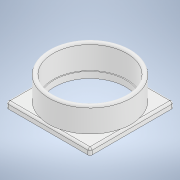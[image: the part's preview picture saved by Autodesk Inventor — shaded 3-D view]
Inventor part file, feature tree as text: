
AUTODESK INVENTOR PART (.ipt)
format: ipt  version: 2022 (Build 260153000, 153)  size: 171,520 bytes
history: native  units: in
note: dims shown in document units (in); Inventor stores cm internally (conversion verified against a paired STEP export)
features: extrude x3, sketch x3, fillet x2
ambient origin geometry x8: Origin, YZ Plane, XZ Plane, XY Plane, X Axis, Y Axis, Z Axis, Center Point
bodies: Solid1 (feature_tree)
feature tree (8):
  extrude  "Extrusion1"  Depth=2.5625in
  extrude  "Extrusion2"  Depth=0.1875in
  extrude  "Extrusion3"  Depth=0.0625in TaperAngle=0.0deg
  fillet  "Fillet1"  [1 undecoded]
  fillet  "Fillet2"  Radius=0.0625in
  sketch  "Sketch1"  dims[d0=2.5625in d1=2.5625in]
  sketch  "Sketch2"  dims[d2=0.1875in d3=0.0in d4=2.25in]
  sketch  "Sketch3"  dims[d5=0.125in d6=0.75in d7=0.0in d8=0.0in d9=0.0in d10=0.0625in d11=0.0625in d12=2.1875in]
note: 1 required parameter value undecoded (feature->parameter linkage not recoverable at this tier; creation-order binding heuristic only, values carry confidence <= 0.55)
